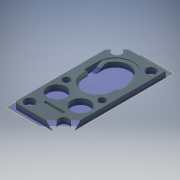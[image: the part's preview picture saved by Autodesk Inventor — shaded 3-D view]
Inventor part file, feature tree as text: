
AUTODESK INVENTOR PART (.ipt)
format: ipt  version: 2016 (Build 200138000, 138)  size: 489,984 bytes
history: native  units: mm
features: extrude x10, sketch x9, projected_geometry x9, chamfer x6, thicken_offset x3, reference x3, plane x2, fillet x2, hole x1
ambient origin geometry x8: Origin, YZ Plane, XZ Plane, XY Plane, X Axis, Y Axis, Z Axis, Center Point
bodies: Solid1 (feature_tree)
feature tree (45):
  sketch  "Sketch2"  dims[d6=10.0mm d7=0.0mm d8=31.25mm]
  plane  "Work Plane3"
  extrude  "Extrusion1"  Depth=31.25mm
  extrude  "Extrusion2"  Depth=14.0mm
  plane  "Work Plane2"
  extrude  "Extrusion3"  TaperAngle=0.0deg  [1 undecoded]
  extrude  "Extrusion4"  Depth=82.0mm
  extrude  "Extrusion5"  Depth=31.25mm
  extrude  "Extrusion6"  TaperAngle=0.0deg  [1 undecoded]
  chamfer  "Chamfer1"  [1 undecoded]
  chamfer  "Chamfer2"  Distance=3.0mm
  extrude  "Extrusion10"  TaperAngle=0.0deg  [1 undecoded]
  extrude  "Extrusion11"  Depth=12.0mm
  chamfer  "Chamfer4"  Distance=3.0mm
  extrude  "Extrusion7"  TaperAngle=45.0deg  [1 undecoded]
  chamfer  "Chamfer3"  Distance=8.4mm
  hole  "Hole1"  [1 undecoded]
  thicken_offset  "Thicken2"
  thicken_offset  "Thicken3"
  extrude  "Extrusion9"  TaperAngle=45.0deg  [1 undecoded]
  chamfer  "Chamfer5"  Distance=6.0mm
  fillet  "Fillet2"  Radius=3.0mm
  fillet  "Fillet3"  [1 undecoded]
  thicken_offset  "Thicken4"
  chamfer  "Chamfer6"  Distance=1.5mm
  sketch  "Sketch3"  dims[d9=14.0mm d10=14.0mm]
  sketch  "Sketch4"  dims[d11=3.0mm d12=0.0mm]
  sketch  "Sketch5"  dims[d13=-6.0mm d14=82.0mm]
  sketch  "Sketch6"  dims[d15=14.0mm d16=31.25mm]
  sketch  "Sketch7"  dims[d17=3.0mm d18=0.0mm]
  sketch  "Sketch8"  dims[d20=3.0mm]
  reference  "Reference24"
  sketch  "Sketch11"  dims[d21=0.0mm]
  sketch  "Sketch13"  dims[d23=3.0mm d24=0.0mm d25=3.0mm d26=0.0mm d27=8.4mm d28=3.0mm d29=45.0deg d30=8.4mm d31=3.0mm d32=45.0deg d33=6.0mm d34=3.0mm d35=0.0mm d36=1.5mm d37=3.0mm d38=45.0deg d47=3.0mm d48=6.0mm d49=4.0mm d50=2.0mm d51=90.0deg d52=8.0mm d53=20.594885mm d87=3.0mm d88=0.0mm d89=0.75mm d90=3.0mm d91=45.0deg d93=9.0mm d95=10.0mm d96=0.0mm d97=10.0mm d98=0.0mm d99=3.0mm d100=3.0mm d101=41.0mm d103=1.4mm d104=1.4mm d106=1.4mm d107=0.7mm d109=6.0mm d110=6.0mm d111=2.0mm d112=45.0deg d113=5.585054mm d114=0.6mm d115=12.0mm d116=0.5mm d117=0.5mm d118=4.5mm d119=2.0mm d120=45.0deg]
  projected_geometry  "Projected Loop4"
  projected_geometry  "Projected Loop5"
  projected_geometry  "Projected Loop8"
  reference  "Reference26"
  projected_geometry  "Projected Loop9"
  projected_geometry  "Projected Loop15"
  reference  "Reference27"
  projected_geometry  "Projected Loop17"
  projected_geometry  "Projected Loop18"
  projected_geometry  "Projected Loop19"
  projected_geometry  "Projected Loop20"
note: 8 required parameter values undecoded (feature->parameter linkage not recoverable at this tier; creation-order binding heuristic only, values carry confidence <= 0.55)
